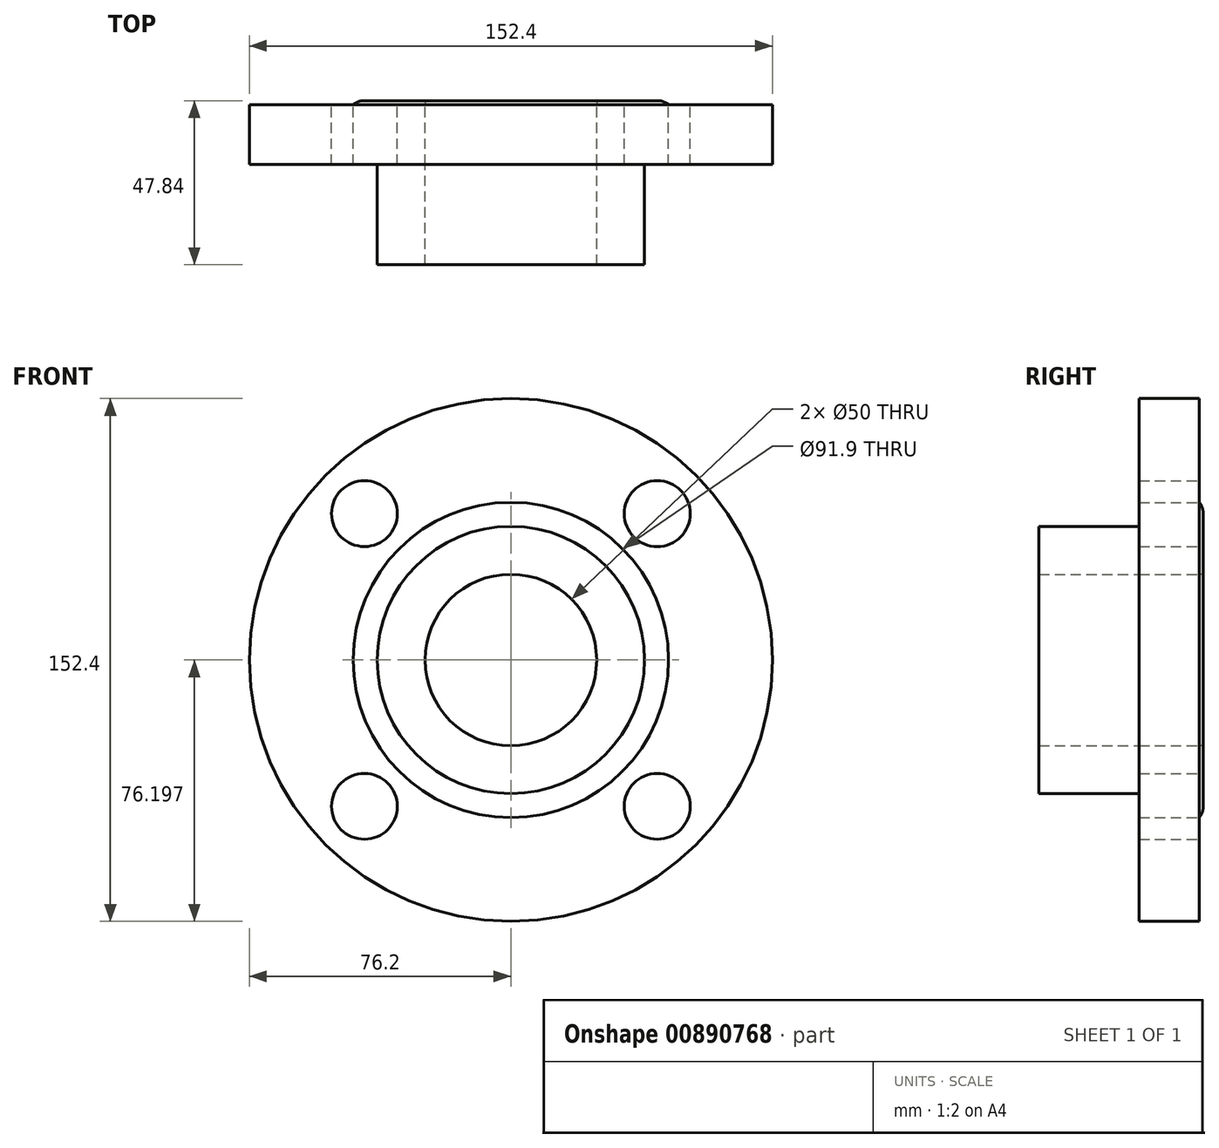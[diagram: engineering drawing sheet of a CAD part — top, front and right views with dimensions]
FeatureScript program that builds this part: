
annotation { "Feature Type Name" : "Feature", "Feature Type Description" : "" }
export const myFeature = defineFeature(function(context is Context, id is Id, definition is map)
    precondition{}
    {
        {
            var Q0;
            Q0=qCreatedBy(makeId("Front.planeOp"),FACE);
            var sketch = newSketch(context, id + "F0", { "sketchPlane" : qUnion([Q0])});
            skCircle(sketch, "E0", {"center": v(-231.6, 1.04) * mm, "radius": 76.2 * mm});
            skCircle(sketch, "E1", {"center": v(-231.6, 1.04) * mm, "radius": 45.95 * mm});
            skCircle(sketch, "E2", {"center": v(-231.6, 1.04) * mm, "radius": 25 * mm});
            skCircle(sketch, "E3", {"center": v(-274.26, 43.7) * mm, "radius": 9.6 * mm});
            skCircle(sketch, "E4", {"center": v(-274.26, -41.61) * mm, "radius": 9.6 * mm});
            skCircle(sketch, "E5", {"center": v(-188.95, 43.7) * mm, "radius": 9.6 * mm});
            skCircle(sketch, "E6", {"center": v(-188.95, -41.61) * mm, "radius": 9.6 * mm});
            skSolve(sketch);
        }
        {
            var Q0;
            Q0=makeQuery(id+"F0.imprint","IMPRINT",FACE,{"disambiguationData":[TD([[makeQuery(id+"F0.imprint","IMPRINT",EDGE,{"derivedFrom":sQuery(id+"F0.wireOp",EDGE,"E0")}),1.0]])]});
            extrude(context, id + "F1", {"entities" : qUnion([Q0]), "depth" : 17.5 * mm, "offsetDistance" : 25.4 * mm});
        }
        {
            var Q0;
            Q0=makeQuery(id+"F0.imprint","IMPRINT",FACE,{"disambiguationData":[TD([[makeQuery(id+"F0.imprint","IMPRINT",EDGE,{"derivedFrom":sQuery(id+"F0.wireOp",EDGE,"E1")}),1.0]])]});
            extrude(context, id + "F2", {"entities" : qUnion([Q0]), "operationType" : NewBodyOperationType.ADD, "oppositeDirection" : true, "depth" : 1.14 * mm, "offsetDistance" : 25.4 * mm});
        }
        {
            var Q0;
            Q0=makeQuery(id+"F2.opExtrude","CAP_EDGE",EDGE,{"disambiguationData":[OSD([sQuery(id+"F0.wireOp",EDGE,"E1")])],"isStart":false});
            fillet(context, id + "F3", {"entities" : qUnion([Q0]), "radius" : 5.08 * mm, "tangentPropagation" : true, "allowEdgeOverflow" : false});
        }
        {
            var Q0;
            Q0=makeQuery(id+"F1.opExtrude","CAP_FACE",FACE,{"disambiguationData":[OSD([sQuery(id+"F0.wireOp",EDGE,"E0"),sQuery(id+"F0.wireOp",EDGE,"E1"),sQuery(id+"F0.wireOp",EDGE,"E3"),sQuery(id+"F0.wireOp",EDGE,"E4"),sQuery(id+"F0.wireOp",EDGE,"E5"),sQuery(id+"F0.wireOp",EDGE,"E6")])],"isStart":false});
            var sketch = newSketch(context, id + "F4", { "sketchPlane" : qUnion([Q0])});
            skCircle(sketch, "E7", {"center": v(-231.6, 1.04) * mm, "radius": 38.95 * mm});
            skCircle(sketch, "E8", {"center": v(-231.6, 1.04) * mm, "radius": 25 * mm});
            skSolve(sketch);
        }
        {
            var Q0;
            Q0=makeQuery(id+"F4.imprint","IMPRINT",FACE,{"disambiguationData":[TD([[makeQuery(id+"F4.imprint","IMPRINT",EDGE,{"derivedFrom":sQuery(id+"F4.wireOp",EDGE,"E7")}),1.0]])]});
            extrude(context, id + "F5", {"entities" : qUnion([Q0]), "depth" : 29.2 * mm, "offsetDistance" : 25.4 * mm});
        }
        {
            var Q0;
            Q0=makeQuery(id+"F0.imprint","IMPRINT",FACE,{"disambiguationData":[TD([[makeQuery(id+"F0.imprint","IMPRINT",EDGE,{"derivedFrom":sQuery(id+"F0.wireOp",EDGE,"E1")}),1.0]])]});
            extrude(context, id + "F6", {"entities" : qUnion([Q0]), "depth" : 17.5 * mm, "offsetDistance" : 25.4 * mm});
        }
    });
